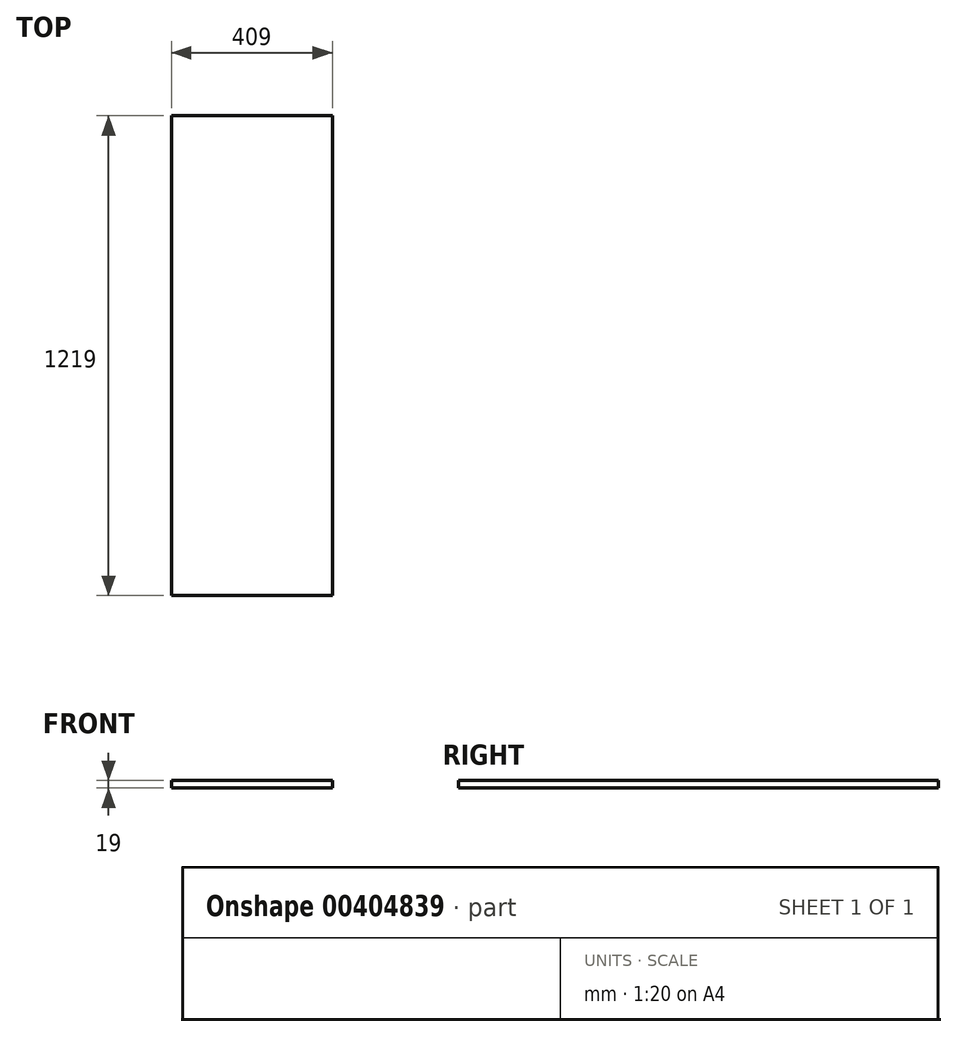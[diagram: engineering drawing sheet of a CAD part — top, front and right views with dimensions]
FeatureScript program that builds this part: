
annotation { "Feature Type Name" : "Feature", "Feature Type Description" : "" }
export const myFeature = defineFeature(function(context is Context, id is Id, definition is map)
    precondition{}
    {
        {
            var Q0;
            Q0=qCreatedBy(makeId("Top.planeOp"),FACE);
            var sketch = newSketch(context, id + "F0", { "sketchPlane" : qUnion([Q0])});
            skLineSegment(sketch, "E0.bottom", {"start": v(-204.5, 609.5) * mm, "end": v(204.5, 609.5) * mm});
            skLineSegment(sketch, "E0.top", {"start": v(-204.5, -609.5) * mm, "end": v(204.5, -609.5) * mm});
            skLineSegment(sketch, "E0.left", {"start": v(-204.5, 609.5) * mm, "end": v(-204.5, -609.5) * mm});
            skLineSegment(sketch, "E0.right", {"start": v(204.5, 609.5) * mm, "end": v(204.5, -609.5) * mm});
            skPoint(sketch, "E0.middle", {"position": v(0, 0) * mm});
            skSolve(sketch);
        }
        {
            var Q0;
            Q0 = qSketchRegion(id + "F0", true);
            extrude(context, id + "F1", {"entities" : qUnion([Q0]), "depth" : 19 * mm});
        }
    });
